SOLIDWORKS PART (.sldprt)
format: sldprt  version: not decoded by parser v0  size: 4,597,248 bytes
history: native  units: mm
features: sketch x10, plane x6, extrude x5, revolve x5, pattern_linear x5, pattern_circular x5 + 1 further entry (+6 scaffold rows collapsed)
feature tree (43):
  scaffold x6  (default folders/planes/origin — collapsed)
  "Corps de surface"
  plane  "Face"
  plane  "Dessus"
  plane  "Droite"
  plane  "Plan1"  Offset=12.8mm
  sketch  "Esquisse3"  dims[D1=48.0mm D2=30.0mm]
  extrude  "Lien1"  Depth=0.1mm
  sketch  "Esquisse1"  dims[c1.D1=~22.25387mm c2.D1=20.0deg c2.D2=10.0mm c2.D3=3.0mm c2.D4=0.4mm c3.D1=0.4mm c3.D2=10.0mm c3.D3=3.0mm c3.D4=~3.564141mm c4.D4=20.0deg c4.D5=15.0mm]
  revolve  "effort1"  Angle=360deg
  pattern_linear  "Répétition linéaire1"  Count1=3 Count2=1 Spacing1=4mm Spacing2=50mm
  pattern_circular  "Répétition circulaire2"  Count=18 Angle=20deg
  plane  "Plan2"  Offset=10mm
  sketch  "Esquisse4"  dims[D1=30.0mm D2=81.0mm]
  extrude  "Lien2"  Depth=0.1mm
  sketch  "Esquisse5"  dims[c1.D1=10.0mm c1.D2=0.4mm c1.D3=3.0mm c1.D4=~4.553505mm c2.D4=20.0deg c2.D5=10.0mm c2.D6=25.0mm]
  revolve  "effort2"  Angle=360deg
  pattern_linear  "Répétition linéaire3"  Count1=4 Count2=1 Spacing1=4mm Spacing2=50mm
  pattern_circular  "Répétition circulaire3"  Count=24 Angle=15deg
  plane  "Plan3"  Offset=7mm
  sketch  "Esquisse6"  dims[D1=30.0mm]
  extrude  "Lien3"  Depth=11mm
  sketch  "Esquisse7"  dims[c1.D1=0.4mm c1.D2=10.0mm c1.D3=3.0mm c1.D4=~3.837755mm c2.D4=20.0deg c2.D5=7.0mm]
  revolve  "Révolution3"  Angle=360deg
  pattern_linear  "Répétition linéaire5"  Count1=3 Count2=1 Spacing1=5mm Spacing2=50mm
  pattern_circular  "Répétition circulaire4"  Count=12 Angle=30deg
  sketch  "Esquisse10"  dims[D1=81.0mm D2=80.0mm]
  extrude  "Lien4"  Depth=90mm
  sketch  "Esquisse9"  dims[c1.D1=0.4mm c1.D2=10.0mm c1.D3=3.0mm c1.D4=~3.761909mm c2.D4=20.0deg c2.D5=40.1mm]
  revolve  "Révolution4"  Angle=360deg
  pattern_circular  "Répétition circulaire5"  Count=24 Angle=15deg
  pattern_linear  "Répétition linéaire8"  Count1=7 Count2=1 Spacing1=10mm Spacing2=50mm
  sketch  "Esquisse11"  dims[D1=35.0mm]
  extrude  "Lien5"  Depth=0.1mm
  sketch  "Esquisse12"  dims[c1.D1=20.0mm c1.D2=10.0mm c1.D3=0.4mm c1.D4=3.0mm c1.D5=~3.419668mm c2.D5=20.0deg]
  revolve  "Révolution5"  Angle=360deg
  pattern_linear  "Répétition linéaire9"  Count1=5 Count2=1 Spacing1=4mm Spacing2=50mm
  pattern_circular  "Répétition circulaire6"  Count=18 Angle=20deg
decode coverage: 30 of 30 modeling features carry decoded parameters; 1 rows unclassified (native names shown)
note: ~ marks probable driven/reference dimensions
note: suppression state not decoded; provenance and decode notes live in map.json
